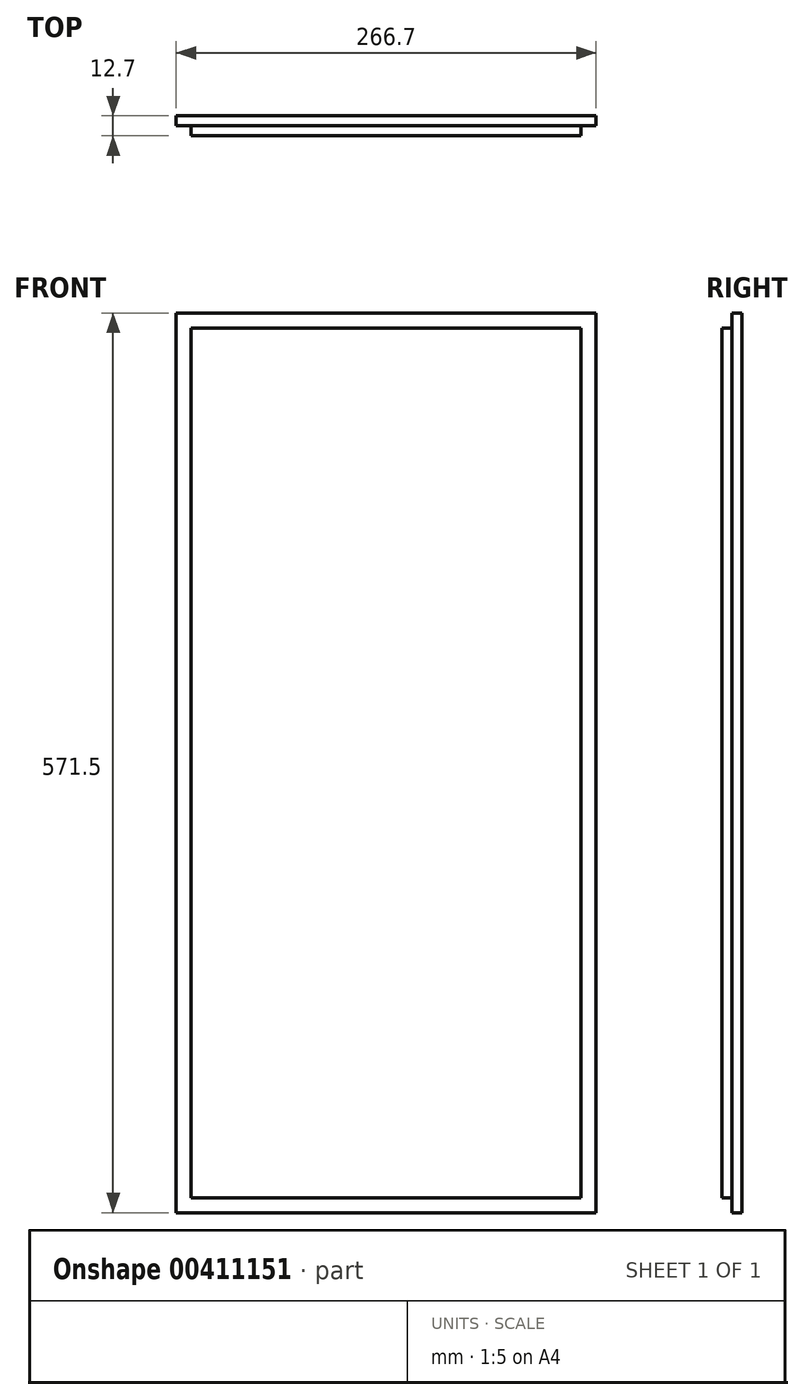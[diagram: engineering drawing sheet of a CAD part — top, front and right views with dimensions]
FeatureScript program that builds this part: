
annotation { "Feature Type Name" : "Feature", "Feature Type Description" : "" }
export const myFeature = defineFeature(function(context is Context, id is Id, definition is map)
    precondition{}
    {
        {
            var Q0;
            Q0=qCreatedBy(makeId("Front.planeOp"),FACE);
            var sketch = newSketch(context, id + "F0", { "sketchPlane" : qUnion([Q0])});
            skLineSegment(sketch, "E0.bottom", {"start": v(0, 0) * mm, "end": v(266.7, 0) * mm});
            skLineSegment(sketch, "E0.top", {"start": v(0, -571.5) * mm, "end": v(266.7, -571.5) * mm});
            skLineSegment(sketch, "E0.left", {"start": v(0, 0) * mm, "end": v(0, -571.5) * mm});
            skLineSegment(sketch, "E0.right", {"start": v(266.7, 0) * mm, "end": v(266.7, -571.5) * mm});
            skLineSegment(sketch, "E1.bottom", {"start": v(9.53, -9.53) * mm, "end": v(257.17, -9.53) * mm});
            skLineSegment(sketch, "E1.top", {"start": v(9.53, -561.98) * mm, "end": v(257.18, -561.98) * mm});
            skLineSegment(sketch, "E1.left", {"start": v(9.53, -9.52) * mm, "end": v(9.53, -561.98) * mm});
            skLineSegment(sketch, "E1.right", {"start": v(257.18, -9.52) * mm, "end": v(257.18, -561.98) * mm});
            skSolve(sketch);
        }
        {
            var Q0;
            Q0 = qSketchRegion(id + "F0", true);
            var Q1;
            Q1=makeQuery(id+"F0.imprint","IMPRINT",FACE,{"disambiguationData":[TD([[makeQuery(id+"F0.imprint","IMPRINT",EDGE,{"derivedFrom":sQuery(id+"F0.wireOp",EDGE,"E1.bottom")}),-1.0]])]});
            extrude(context, id + "F1", {"entities" : qUnion([Q0, Q1]), "oppositeDirection" : true, "depth" : 6.35 * mm});
        }
        {
            var Q0;
            Q0=makeQuery(id+"F0.imprint","IMPRINT",FACE,{"disambiguationData":[TD([[makeQuery(id+"F0.imprint","IMPRINT",EDGE,{"derivedFrom":sQuery(id+"F0.wireOp",EDGE,"E1.bottom")}),-1.0]])]});
            extrude(context, id + "F2", {"entities" : qUnion([Q0]), "operationType" : NewBodyOperationType.ADD, "depth" : 6.35 * mm});
        }
    });
